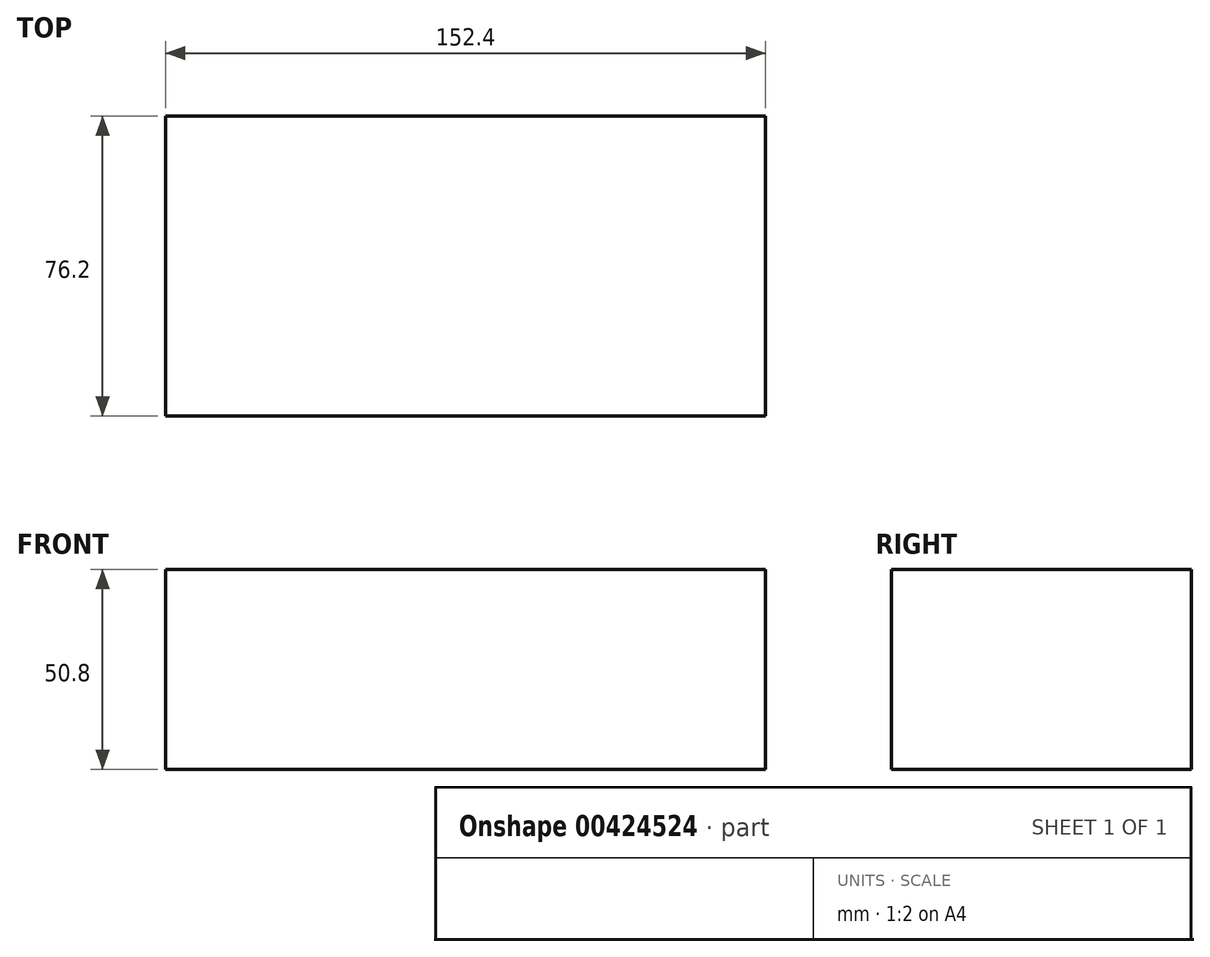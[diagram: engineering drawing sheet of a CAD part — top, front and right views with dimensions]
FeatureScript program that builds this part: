
annotation { "Feature Type Name" : "Feature", "Feature Type Description" : "" }
export const myFeature = defineFeature(function(context is Context, id is Id, definition is map)
    precondition{}
    {
        {
            var Q0;
            Q0=qCreatedBy(makeId("Front.planeOp"),FACE);
            var sketch = newSketch(context, id + "F0", { "sketchPlane" : qUnion([Q0])});
            skLineSegment(sketch, "E0", {"start": v(-76.33, 0) * mm, "end": v(76.07, 0) * mm});
            skLineSegment(sketch, "E1", {"start": v(-76.33, 0) * mm, "end": v(-76.33, 50.8) * mm});
            skLineSegment(sketch, "E2", {"start": v(76.07, 0) * mm, "end": v(76.07, 50.8) * mm});
            skLineSegment(sketch, "E3", {"start": v(76.07, 50.8) * mm, "end": v(-76.33, 50.8) * mm});
            skSolve(sketch);
        }
        {
            var Q0;
            Q0 = qSketchRegion(id + "F0", true);
            extrude(context, id + "F1", {"entities" : qUnion([Q0]), "depth" : 76.2 * mm});
        }
    });
